# Revit family: 4054892
name_source: partatom
category: Lighting Fixtures
revit_build: Autodesk Revit 2018 (Build: 20170223_1515(x64)
units: mm (PartAtom-declared; Revit-internal decimal feet)

## family parameters
Cut with Voids When Loaded = No
Host = Face
Light Source = Yes
OmniClass Number = 23.80.70.11.17
OmniClass Title = Specialized Lighting by Location or Use
Part Type = Normal
Room Calculation Point = No
Round Connector Dimension = Use Diameter
Shared = No

## types (1)
- CASSINI PLANAR 400 1229LM 830 DA EM3 WH
    Apparent Load = 11 VA
    Assembly Code = D5020200
    Body Material = Aluminium Brushed_Body_Sylvania
    Catalog Number = 4055052 Cassini Planar 4000K 400mm
    Color Filter = 16777215
    Default Elevation = 0 mm  [stored 0 ft]
    Diameter = 400 mm  [stored 1.31234 ft]
    Diffuser Material = Acrylic_Opal_Reflector_Sylvania_White
    Dimming Lamp Color Temperature Shift = <None>
    Drive Current = 700 mA
    Emit Shape Visible in Rendering = No
    Emit from Circle Diameter = 264 mm  [stored 0.866142 ft]
    Height = 90 mm  [stored 0.295276 ft]
    IK Rating = 10
    Lamp = 11.20 W LED
    Lamp Comments = Integrated LED, Samsung 2323 LED 11.2W
    Manufacturer = Feilo Sylvania
    Model = Significant energy savings compared to traditional CFL and 2D
fixtures. Excellent flashing provides perfect homogenous light
distribution . Unique feature allowing a choice between High Output or
High efficiency with the flick of a switch. 50,000 hours life, providing a
maintenance free lighting solution.
    Photometric Web File = 4054892.ies
    Product Family = Cassini Planar LED
    Product Page URL = http://www.feilosylvania.com
    Radius = 200 mm  [stored 0.656168 ft]
    Radius Diffuser = 132 mm  [stored 0.433071 ft]
    Tilt Angle = -90.00°
    URL = http://www.feilosylvania.com
    Voltage = 230 V
    Voltage Comments = UNV (Universal Voltage; 220-240 Volt)
    Wattage Comments = 17
    Weight = 1.10 kg

note: [stored X ft] marks values corroborated as IEEE doubles in the binary element streams (Revit-internal decimal feet)

## geometry (parser evidence)
native form markers: Blend x9, Sweep x5
no freeform markers — native parametric forms only
